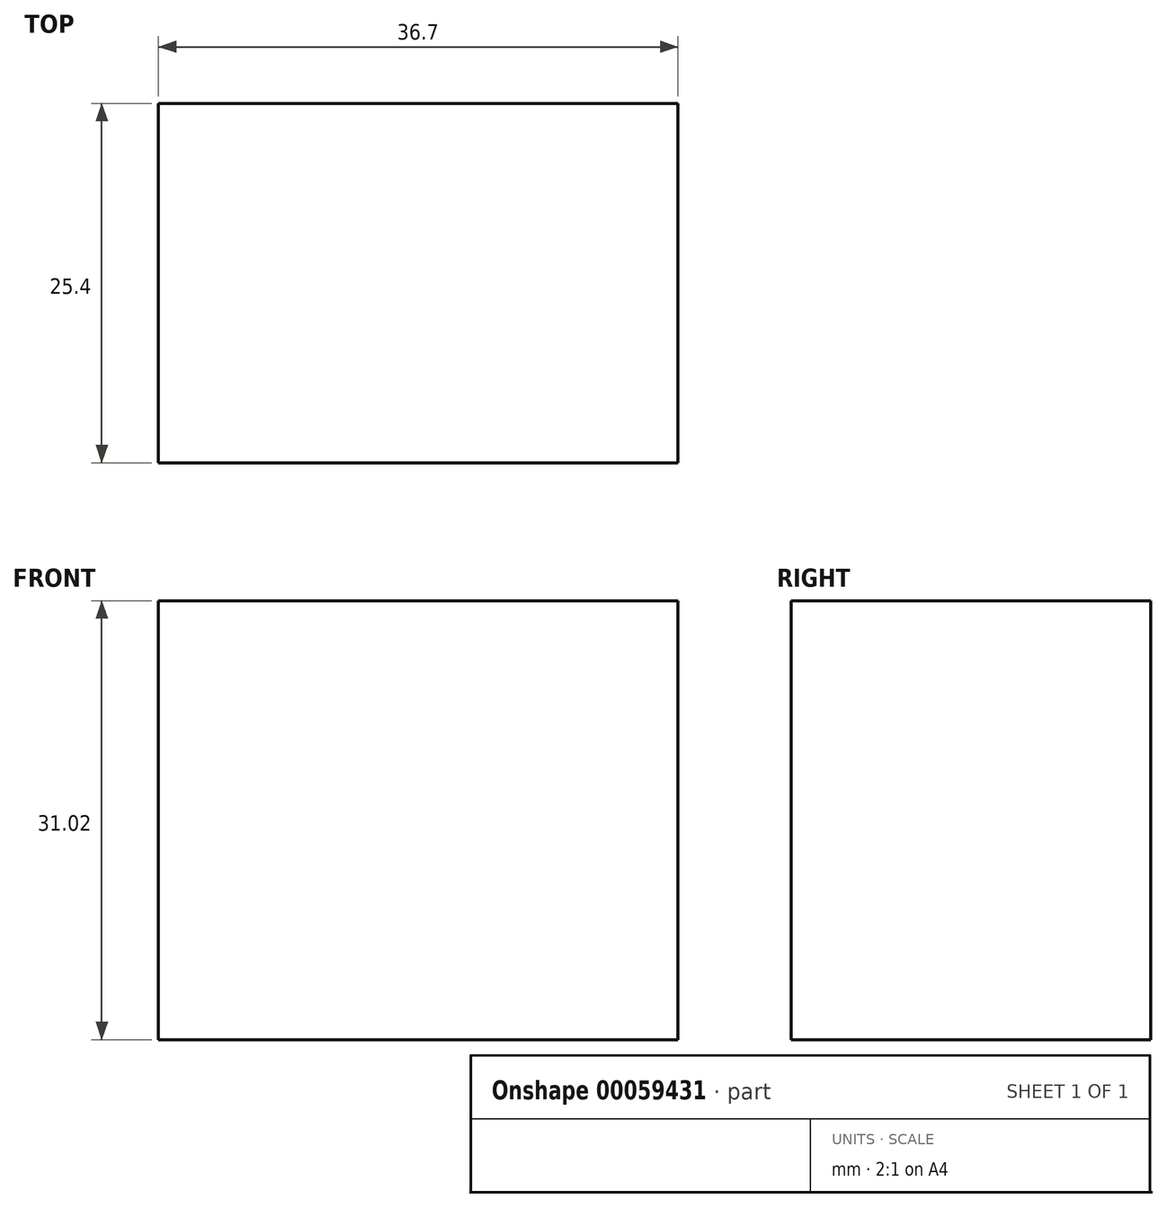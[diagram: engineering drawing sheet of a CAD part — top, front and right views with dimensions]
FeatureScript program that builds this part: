
annotation { "Feature Type Name" : "Feature", "Feature Type Description" : "" }
export const myFeature = defineFeature(function(context is Context, id is Id, definition is map)
    precondition{}
    {
        {
            var Q0;
            Q0=qCreatedBy(makeId("Front.planeOp"),FACE);
            var sketch = newSketch(context, id + "F0", { "sketchPlane" : qUnion([Q0])});
            skLineSegment(sketch, "E0.bottom", {"start": v(0, 0) * mm, "end": v(36.7, 0) * mm});
            skLineSegment(sketch, "E0.top", {"start": v(0, 31.02) * mm, "end": v(36.7, 31.02) * mm});
            skLineSegment(sketch, "E0.left", {"start": v(0, 0) * mm, "end": v(0, 31.02) * mm});
            skLineSegment(sketch, "E0.right", {"start": v(36.7, 0) * mm, "end": v(36.7, 31.02) * mm});
            skSolve(sketch);
        }
        {
            var Q0;
            Q0 = qSketchRegion(id + "F0", true);
            extrude(context, id + "F1", {"entities" : qUnion([Q0]), "depth" : 25.4 * mm});
        }
    });
